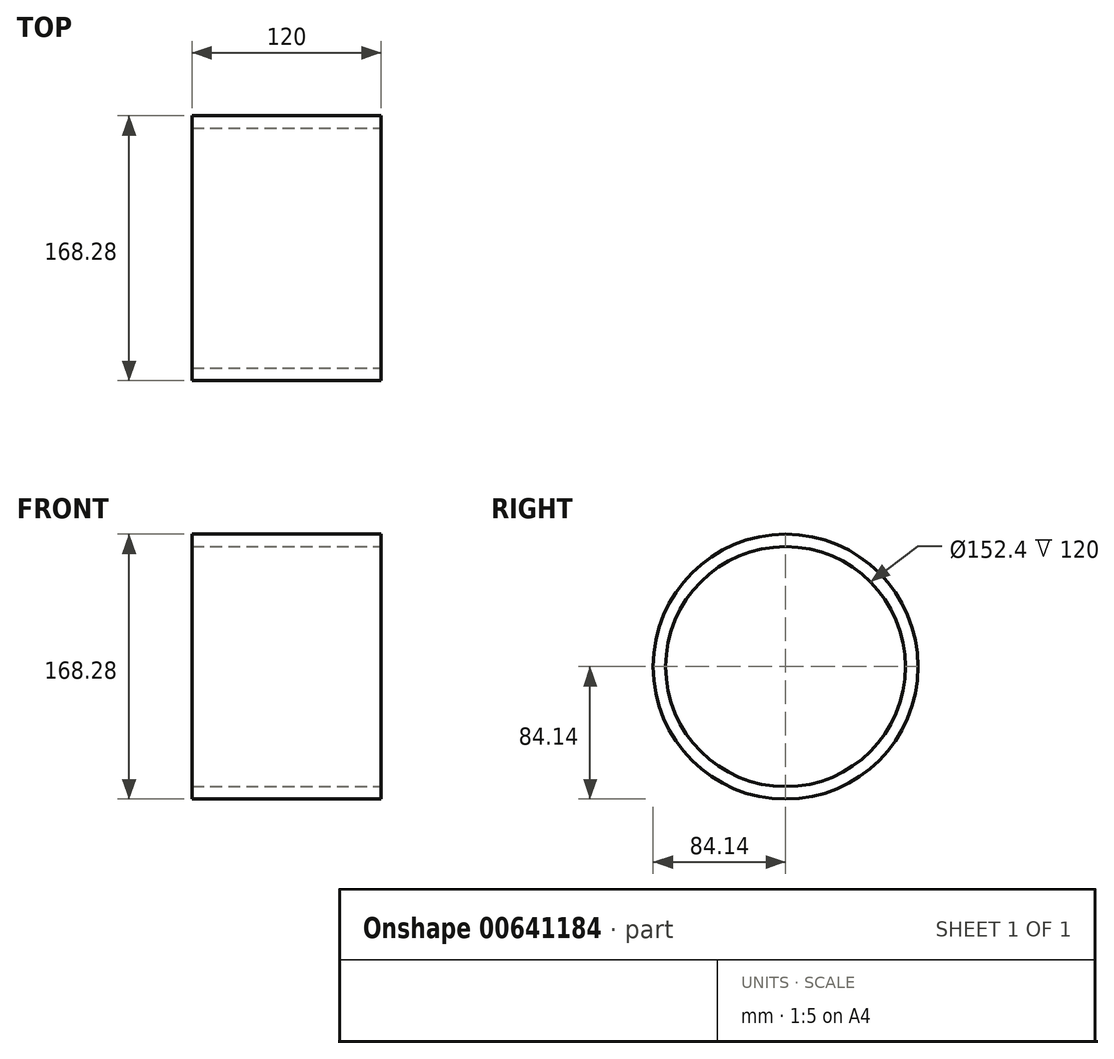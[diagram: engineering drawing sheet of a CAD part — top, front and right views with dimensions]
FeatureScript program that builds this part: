
annotation { "Feature Type Name" : "Feature", "Feature Type Description" : "" }
export const myFeature = defineFeature(function(context is Context, id is Id, definition is map)
    precondition{}
    {
        {
            assignVariable(context, id + "F0", {"name" : "BL", "anyValue" : 120});
        }
        {
            var Q0;
            Q0=qCreatedBy(makeId("Right.planeOp"),FACE);
            var sketch = newSketch(context, id + "F1", { "sketchPlane" : qUnion([Q0])});
            skCircle(sketch, "E0", {"center": v(0, 0) * mm, "radius": 84.14 * mm});
            skCircle(sketch, "E1", {"center": v(0, 0) * mm, "radius": 76.2 * mm});
            skSolve(sketch);
        }
        {
            var Q0;
            Q0=makeQuery(id+"F1.imprint","IMPRINT",FACE,{"disambiguationData":[TD([[makeQuery(id+"F1.imprint","IMPRINT",EDGE,{"derivedFrom":sQuery(id+"F1.wireOp",EDGE,"E0")}),1.0]])]});
            extrude(context, id + "F2", {"entities" : qUnion([Q0]), "oppositeDirection" : true, "depth" : (getVariable(context, 'BL')) * mm, "offsetDistance" : 25.4 * mm});
        }
    });
